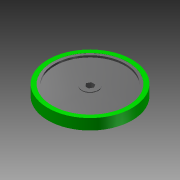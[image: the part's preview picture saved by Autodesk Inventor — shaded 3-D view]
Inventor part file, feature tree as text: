
AUTODESK INVENTOR PART (.ipt)
format: ipt  version: 2012 (Build 160160000, 160)  size: 125,440 bytes
history: native  units: mm
features: extrude x5, sketch x1
ambient origin geometry x8: Origin, YZ Plane, XZ Plane, XY Plane, X Axis, Y Axis, Z Axis, Center Point
bodies: Solid1 (feature_tree)
feature tree (6):
  sketch  "Sketch1"  dims[d0=8.0mm d2=12.7mm d3=12.7mm d4=0.0mm d5=20.32mm d6=0.0mm d7=158.75mm d8=13.0mm d9=10.0mm d10=0.0mm d11=10.0mm d12=0.0mm d13=31.0mm d14=15.24mm d15=0.0mm]
  extrude  "Extrusion1"  Depth=12.7mm
  extrude  "Extrusion2"  Depth=12.7mm TaperAngle=0.0deg
  extrude  "Extrusion3"  Depth=20.32mm TaperAngle=0.0deg
  extrude  "Extrusion4"  Depth=158.75mm
  extrude  "Extrusion5"  Depth=13.0mm
